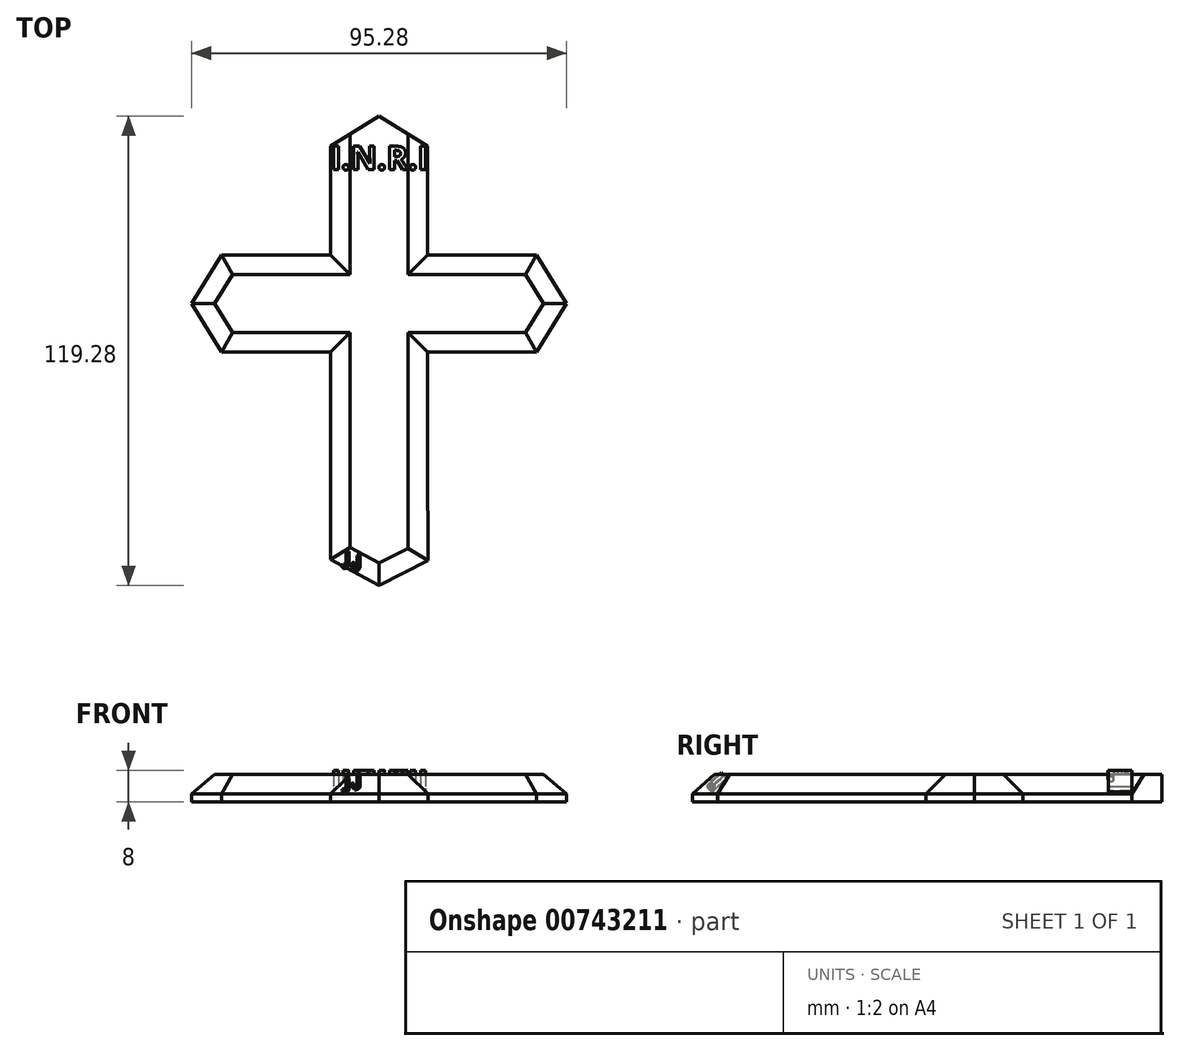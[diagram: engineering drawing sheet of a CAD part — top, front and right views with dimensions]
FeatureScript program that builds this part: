
annotation { "Feature Type Name" : "Feature", "Feature Type Description" : "" }
export const myFeature = defineFeature(function(context is Context, id is Id, definition is map)
    precondition{}
    {
        {
            var Q0;
            Q0=qCreatedBy(makeId("Top.planeOp"),FACE);
            var sketch = newSketch(context, id + "F0", { "sketchPlane" : qUnion([Q0])});
            skLineSegment(sketch, "E0", {"start": v(-12.33, 12.33) * mm, "end": v(-12.33, 40) * mm});
            skLineSegment(sketch, "E1", {"start": v(-12.33, 40) * mm, "end": v(0, 47.64) * mm});
            skLineSegment(sketch, "E2", {"start": v(0, 47.64) * mm, "end": v(12.33, 40) * mm});
            skLineSegment(sketch, "E3", {"start": v(12.33, 40) * mm, "end": v(12.33, 12.33) * mm});
            skLineSegment(sketch, "E4.1.0", {"start": v(-40, 12.33) * mm, "end": v(-12.33, 12.33) * mm});
            skLineSegment(sketch, "E4.2.0", {"start": v(-12.33, -40) * mm, "end": v(-12.33, -12.33) * mm});
            skLineSegment(sketch, "E4.3.0", {"start": v(40, -12.33) * mm, "end": v(12.33, -12.33) * mm});
            skPoint(sketch, "E4.center", {"position": v(0, 0) * mm});
            skLineSegment(sketch, "E5.1.0", {"start": v(-47.64, 0) * mm, "end": v(-40, 12.33) * mm});
            skLineSegment(sketch, "E5.3.0", {"start": v(47.64, 0) * mm, "end": v(40, -12.33) * mm});
            skLineSegment(sketch, "E6.1.0", {"start": v(-40, -12.33) * mm, "end": v(-47.64, 0) * mm});
            skLineSegment(sketch, "E6.3.0", {"start": v(40, 12.33) * mm, "end": v(47.64, 0) * mm});
            skLineSegment(sketch, "E7.1.0", {"start": v(-12.33, -12.33) * mm, "end": v(-40, -12.33) * mm});
            skLineSegment(sketch, "E7.2.0", {"start": v(12.33, -12.33) * mm, "end": v(12.33, -40) * mm});
            skLineSegment(sketch, "E7.3.0", {"start": v(12.33, 12.33) * mm, "end": v(40, 12.33) * mm});
            skLineSegment(sketch, "E8", {"start": v(-12.33, -40) * mm, "end": v(-12.33, -65) * mm});
            skLineSegment(sketch, "E9", {"start": v(-12.33, -65) * mm, "end": v(0, -71.64) * mm});
            skLineSegment(sketch, "E10", {"start": v(0, -71.64) * mm, "end": v(12.45, -65.24) * mm});
            skLineSegment(sketch, "E11", {"start": v(12.45, -65.24) * mm, "end": v(12.33, -40) * mm});
            skPoint(sketch, "E12.orphan", {"position": v(0, 12.33) * mm});
            skPoint(sketch, "E13.orphan", {"position": v(0, -12.33) * mm});
            skPoint(sketch, "E14.orphan", {"position": v(12.33, 0) * mm});
            skPoint(sketch, "E15.orphan", {"position": v(-12.33, 0) * mm});
            skSolve(sketch);
        }
        {
            var Q0;
            Q0=makeQuery(id+"F0.imprint","IMPRINT",FACE,{"disambiguationData":[TD([[makeQuery(id+"F0.imprint","IMPRINT",EDGE,{"derivedFrom":sQuery(id+"F0.wireOp",EDGE,"E0")}),-1.0]])]});
            extrude(context, id + "F1", {"entities" : qUnion([Q0]), "depth" : 7 * mm, "offsetDistance" : 25 * mm});
        }
        {
            var Q0;
            Q0=makeQuery(id+"F1.opExtrude","CAP_FACE",FACE,{"disambiguationData":[OSD([sQuery(id+"F0.wireOp",EDGE,"E0"),sQuery(id+"F0.wireOp",EDGE,"E1"),sQuery(id+"F0.wireOp",EDGE,"E2"),sQuery(id+"F0.wireOp",EDGE,"E3"),sQuery(id+"F0.wireOp",EDGE,"E4.1.0"),sQuery(id+"F0.wireOp",EDGE,"E4.2.0"),sQuery(id+"F0.wireOp",EDGE,"E4.3.0"),sQuery(id+"F0.wireOp",EDGE,"E5.1.0"),sQuery(id+"F0.wireOp",EDGE,"E5.3.0"),sQuery(id+"F0.wireOp",EDGE,"E6.1.0"),sQuery(id+"F0.wireOp",EDGE,"E6.3.0"),sQuery(id+"F0.wireOp",EDGE,"E7.1.0"),sQuery(id+"F0.wireOp",EDGE,"E7.2.0"),sQuery(id+"F0.wireOp",EDGE,"E7.3.0"),sQuery(id+"F0.wireOp",EDGE,"E8"),sQuery(id+"F0.wireOp",EDGE,"E9"),sQuery(id+"F0.wireOp",EDGE,"E10"),sQuery(id+"F0.wireOp",EDGE,"E11")])],"isStart":false});
            var sketch = newSketch(context, id + "F2", { "sketchPlane" : qUnion([Q0])});
            skText(sketch, "E16", { "text": "I.N.R.I", "fontName": "OpenSans-Bold.ttf"});
            const initialGuessF2  = {"E16": [-0.01233, 0.03402, 1, 0, 0.00598]};
            skSetInitialGuess(sketch, initialGuessF2);
            skSolve(sketch);
        }
        {
            var Q0;
            Q0 = qSketchRegion(id + "F2", true);
            extrude(context, id + "F3", {"entities" : qUnion([Q0]), "operationType" : NewBodyOperationType.ADD, "depth" : 1 * mm, "offsetDistance" : 25 * mm});
        }
        {
            var Q0;
            Q0=makeQuery(id+"F1.opExtrude","CAP_EDGE",EDGE,{"disambiguationData":[OSD([sQuery(id+"F0.wireOp",EDGE,"E4.3.0")])],"isStart":false});
            var Q1;
            Q1=makeQuery(id+"F1.opExtrude","CAP_EDGE",EDGE,{"disambiguationData":[OSD([sQuery(id+"F0.wireOp",EDGE,"E7.3.0")])],"isStart":false});
            var Q2;
            Q2=makeQuery(id+"F1.opExtrude","CAP_EDGE",EDGE,{"disambiguationData":[OSD([sQuery(id+"F0.wireOp",EDGE,"E6.3.0")])],"isStart":false});
            var Q3;
            Q3=makeQuery(id+"F1.opExtrude","CAP_EDGE",EDGE,{"disambiguationData":[OSD([sQuery(id+"F0.wireOp",EDGE,"E5.3.0")])],"isStart":false});
            var Q4;
            Q4=makeQuery(id+"F1.opExtrude","CAP_EDGE",EDGE,{"disambiguationData":[OSD([sQuery(id+"F0.wireOp",EDGE,"E5.1.0")])],"isStart":false});
            var Q5;
            Q5=makeQuery(id+"F1.opExtrude","CAP_EDGE",EDGE,{"disambiguationData":[OSD([sQuery(id+"F0.wireOp",EDGE,"E4.1.0")])],"isStart":false});
            var Q6;
            Q6=makeQuery(id+"F1.opExtrude","CAP_EDGE",EDGE,{"disambiguationData":[OSD([sQuery(id+"F0.wireOp",EDGE,"E6.1.0")])],"isStart":false});
            var Q7;
            Q7=makeQuery(id+"F1.opExtrude","CAP_EDGE",EDGE,{"disambiguationData":[OSD([sQuery(id+"F0.wireOp",EDGE,"E7.1.0")])],"isStart":false});
            var Q8;
            Q8=makeQuery(id+"F1.opExtrude","CAP_EDGE",EDGE,{"disambiguationData":[OSD([sQuery(id+"F0.wireOp",EDGE,"E4.2.0"),sQuery(id+"F0.wireOp",EDGE,"E8")])],"isStart":false});
            var Q9;
            Q9=makeQuery(id+"F1.opExtrude","CAP_EDGE",EDGE,{"disambiguationData":[OSD([sQuery(id+"F0.wireOp",EDGE,"E7.2.0")])],"isStart":false});
            var Q10;
            Q10=makeQuery(id+"F1.opExtrude","CAP_EDGE",EDGE,{"disambiguationData":[OSD([sQuery(id+"F0.wireOp",EDGE,"E10")])],"isStart":false});
            var Q11;
            Q11=makeQuery(id+"F1.opExtrude","CAP_EDGE",EDGE,{"disambiguationData":[OSD([sQuery(id+"F0.wireOp",EDGE,"E9")])],"isStart":false});
            var Q12;
            Q12=makeQuery(id+"F1.opExtrude","CAP_EDGE",EDGE,{"disambiguationData":[OSD([sQuery(id+"F0.wireOp",EDGE,"E3")])],"isStart":false});
            var Q13;
            Q13=makeQuery(id+"F1.opExtrude","CAP_EDGE",EDGE,{"disambiguationData":[OSD([sQuery(id+"F0.wireOp",EDGE,"E0")])],"isStart":false});
            chamfer(context, id + "F4", {"entities" : qUnion([Q0, Q1, Q2, Q3, Q4, Q5, Q6, Q7, Q8, Q9, Q10, Q11, Q12, Q13]), "width" : 5 * mm, "tangentPropagation" : true});
        }
        {
            var Q0;
            Q0=makeQuery(id+"F4.opChamfer","BLEND_FACE",FACE,{"disambiguationData":[OSD([sQuery(id+"F0.wireOp",EDGE,"E9")])]});
            var sketch = newSketch(context, id + "F5", { "sketchPlane" : qUnion([Q0])});
            skText(sketch, "E17", { "text": "J.J", "fontName": "OpenSans-Regular.ttf"});
            const initialGuessF5  = {"E17": [0.00726, -0.04742, 1, 0, 0.0041]};
            skSetInitialGuess(sketch, initialGuessF5);
            skSolve(sketch);
        }
        {
            var Q0;
            Q0 = qSketchRegion(id + "F5", true);
            extrude(context, id + "F6", {"entities" : qUnion([Q0]), "operationType" : NewBodyOperationType.ADD, "depth" : 1 * mm, "offsetDistance" : 25 * mm});
        }
    });
